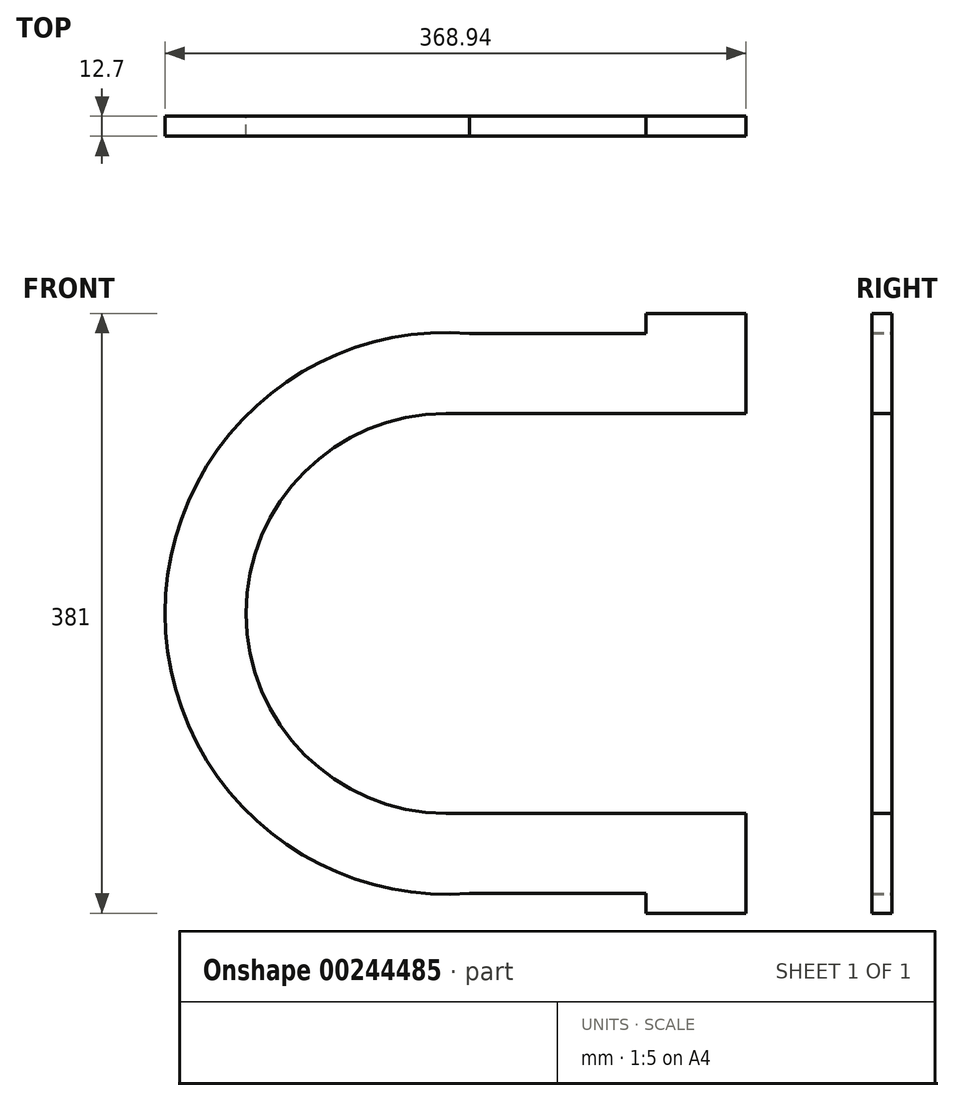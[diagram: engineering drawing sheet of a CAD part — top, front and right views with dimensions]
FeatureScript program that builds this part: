
annotation { "Feature Type Name" : "Feature", "Feature Type Description" : "" }
export const myFeature = defineFeature(function(context is Context, id is Id, definition is map)
    precondition{}
    {
        {
            var Q0;
            Q0=qCreatedBy(makeId("Front.planeOp"),FACE);
            var sketch = newSketch(context, id + "F0", { "sketchPlane" : qUnion([Q0])});
            skLineSegment(sketch, "E0.bottom", {"start": v(127, 177.8) * mm, "end": v(-15.05, 177.8) * mm});
            skLineSegment(sketch, "E0.top", {"start": v(127, -177.8) * mm, "end": v(-15.05, -177.8) * mm});
            skLineSegment(sketch, "E0.left", {"start": v(190.5, 177.8) * mm, "end": v(190.5, 127) * mm});
            skPoint(sketch, "E0.middle", {"position": v(0, 0) * mm});
            skArc(sketch, "E1", {"start": v(0, 127) * mm, "mid": v(-127, 0) * mm, "end": v(0, -127) * mm});
            skLineSegment(sketch, "E2", {"start": v(0, -127) * mm, "end": v(190.5, -127) * mm});
            skLineSegment(sketch, "E3", {"start": v(0, 127) * mm, "end": v(190.5, 127) * mm});
            skLineSegment(sketch, "E4.trimOffspring", {"start": v(190.5, -127) * mm, "end": v(190.5, -177.8) * mm});
            skArc(sketch, "E5", {"start": v(15.05, 177.8) * mm, "mid": v(-178.44, 0) * mm, "end": v(15.05, -177.8) * mm});
            skPoint(sketch, "E0.right.start.orphan", {"position": v(-190.5, 177.8) * mm});
            skPoint(sketch, "E6.orphan", {"position": v(-190.5, -177.8) * mm});
            skLineSegment(sketch, "E7.bottom", {"start": v(190.5, 127) * mm, "end": v(127, 127) * mm});
            skLineSegment(sketch, "E7.top", {"start": v(190.5, 190.5) * mm, "end": v(127, 190.5) * mm});
            skLineSegment(sketch, "E7.left", {"start": v(190.5, 127) * mm, "end": v(190.5, 190.5) * mm});
            skLineSegment(sketch, "E7.right", {"start": v(127, 177.8) * mm, "end": v(127, 190.5) * mm});
            skLineSegment(sketch, "E8.bottom", {"start": v(190.5, -127) * mm, "end": v(127, -127) * mm});
            skLineSegment(sketch, "E8.top", {"start": v(190.5, -190.5) * mm, "end": v(127, -190.5) * mm});
            skLineSegment(sketch, "E8.left", {"start": v(190.5, -127) * mm, "end": v(190.5, -190.5) * mm});
            skLineSegment(sketch, "E8.right", {"start": v(127, -177.8) * mm, "end": v(127, -190.5) * mm});
            skSolve(sketch);
        }
        {
            var Q0;
            Q0 = qSketchRegion(id + "F0", true);
            extrude(context, id + "F1", {"entities" : qUnion([Q0]), "depth" : 12.7 * mm});
        }
    });
